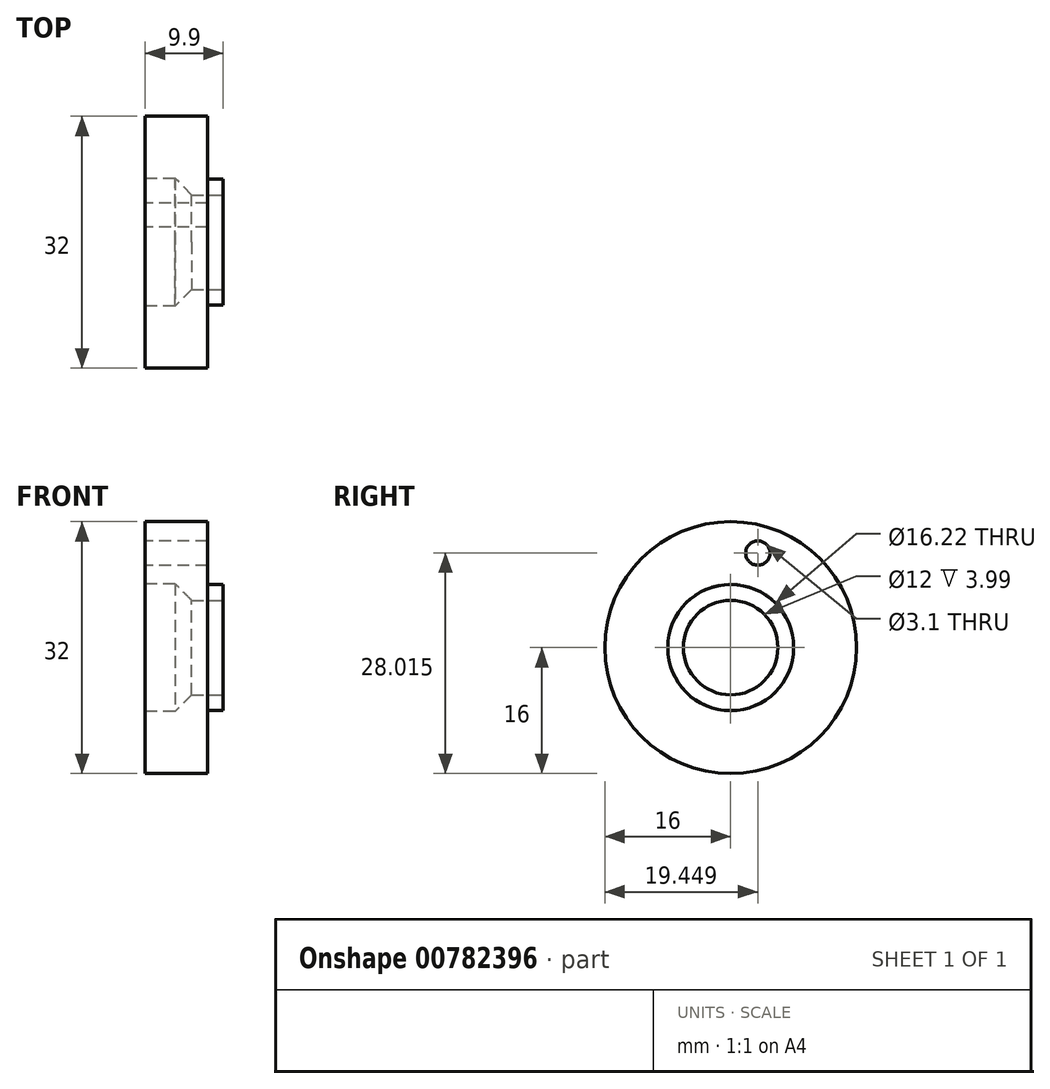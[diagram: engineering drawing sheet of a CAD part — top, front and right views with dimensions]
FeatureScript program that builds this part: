
annotation { "Feature Type Name" : "Feature", "Feature Type Description" : "" }
export const myFeature = defineFeature(function(context is Context, id is Id, definition is map)
    precondition{}
    {
        {
            var Q0;
            Q0=qCreatedBy(makeId("Right.planeOp"),FACE);
            var sketch = newSketch(context, id + "F0", { "sketchPlane" : qUnion([Q0])});
            skCircle(sketch, "E0", {"center": v(0, 0) * mm, "radius": 16 * mm});
            skSolve(sketch);
        }
        {
            var Q0;
            Q0 = qSketchRegion(id + "F0", true);
            extrude(context, id + "F1", {"entities" : qUnion([Q0]), "depth" : 7.9 * mm, "offsetDistance" : 25 * mm});
        }
        {
            var Q0;
            Q0=makeQuery(id+"F1.opExtrude","CAP_FACE",FACE,{"disambiguationData":[OSD([sQuery(id+"F0.wireOp",EDGE,"E0")])],"isStart":true});
            var sketch = newSketch(context, id + "F2", { "sketchPlane" : qUnion([Q0])});
            skCircle(sketch, "E1", {"center": v(0, 0) * mm, "radius": 8.1 * mm});
            skSolve(sketch);
        }
        {
            var Q0;
            Q0 = qSketchRegion(id + "F2", true);
            extrude(context, id + "F3", {"entities" : qUnion([Q0]), "operationType" : NewBodyOperationType.REMOVE, "oppositeDirection" : true, "depth" : 3.8 * mm, "offsetDistance" : 25 * mm});
        }
        {
            var Q0;
            Q0=makeQuery(id+"FPhex85518c5a8B_1.boolean.opBoolean","MERGE",FACE,{"derivedFrom":[makeQuery(id+"F1.opExtrude","CAP_FACE",FACE,{"disambiguationData":[OSD([sQuery(id+"F0.wireOp",EDGE,"E0"),sQuery(id+"F0.wireOp",EDGE,"LPqGSmC4-BEG3-Smh6-pqi2-9UDcotqoIPR3")])],"isStart":false}),makeQuery(id+"FPhex85518c5a8B_1.opExtrude","CAP_FACE",FACE,{"disambiguationData":[OSD([sQuery(id+"F5ubsA8xl3aw4eF_1.wireOp",EDGE,"xLex2xx2-WFXS-E97t-Ro50-xfE8aykVN3Uf")])],"isStart":true})]});
            var sketch = newSketch(context, id + "F4", { "sketchPlane" : qUnion([Q0])});
            skCircle(sketch, "E2", {"center": v(0, 0) * mm, "radius": 6 * mm});
            skSolve(sketch);
        }
        {
            var Q0;
            Q0 = qSketchRegion(id + "F4", true);
            extrude(context, id + "F5", {"entities" : qUnion([Q0]), "operationType" : NewBodyOperationType.REMOVE, "endBound" : BoundingType.THROUGH_ALL, "oppositeDirection" : true, "depth" : 25 * mm, "offsetDistance" : 25 * mm});
        }
        {
            var Q0;
            Q0=makeQuery(id+"F1.opExtrude","CAP_FACE",FACE,{"disambiguationData":[OSD([sQuery(id+"F0.wireOp",EDGE,"E0"),sQuery(id+"F0.wireOp",EDGE,"LPqGSmC4-BEG3-Smh6-pqi2-9UDcotqoIPR3")])],"isStart":true});
            var sketch = newSketch(context, id + "F6", { "sketchPlane" : qUnion([Q0])});
            skCircle(sketch, "E3", {"center": v(0, 0) * mm, "radius": 12.5 * mm, "construction": true});
            skCircle(sketch, "E4", {"center": v(-3.45, 12.01) * mm, "radius": 1.55 * mm});
            skSolve(sketch);
        }
        {
            var Q0;
            Q0=makeQuery(id+"F6.imprint","IMPRINT",FACE,{"disambiguationData":[TD([[makeQuery(id+"F6.imprint","IMPRINT",EDGE,{"derivedFrom":sQuery(id+"F6.wireOp",EDGE,"E4")}),1.0]])]});
            var Q1;
            Q1=sQuery(id+"F6.wireOp",EDGE,"E4");
            extrude(context, id + "F7", {"entities" : qUnion([Q0]), "operationType" : NewBodyOperationType.REMOVE, "surfaceEntities" : qUnion([Q1]), "endBound" : BoundingType.THROUGH_ALL, "oppositeDirection" : true, "depth" : 25 * mm, "offsetDistance" : 25 * mm});
        }
        {
            var Q0;
            Q0=makeQuery(id+"FPhex85518c5a8B_1.boolean.opBoolean","MERGE",FACE,{"derivedFrom":[makeQuery(id+"F1.opExtrude","CAP_FACE",FACE,{"disambiguationData":[OSD([sQuery(id+"F0.wireOp",EDGE,"E0"),sQuery(id+"F0.wireOp",EDGE,"LPqGSmC4-BEG3-Smh6-pqi2-9UDcotqoIPR3")])],"isStart":false}),makeQuery(id+"FPhex85518c5a8B_1.opExtrude","CAP_FACE",FACE,{"disambiguationData":[OSD([sQuery(id+"F5ubsA8xl3aw4eF_1.wireOp",EDGE,"xLex2xx2-WFXS-E97t-Ro50-xfE8aykVN3Uf")])],"isStart":true})]});
            var sketch = newSketch(context, id + "F8", { "sketchPlane" : qUnion([Q0])});
            skCircle(sketch, "E5", {"center": v(0, 0) * mm, "radius": 6 * mm});
            skCircle(sketch, "E6", {"center": v(0, 0) * mm, "radius": 8 * mm});
            skSolve(sketch);
        }
        {
            var Q0;
            Q0=makeQuery(id+"F8.imprint","IMPRINT",FACE,{"disambiguationData":[TD([[makeQuery(id+"F8.imprint","IMPRINT",EDGE,{"derivedFrom":sQuery(id+"F8.wireOp",EDGE,"E5")}),-1.0]])]});
            extrude(context, id + "F9", {"entities" : qUnion([Q0]), "operationType" : NewBodyOperationType.ADD, "depth" : 2 * mm, "offsetDistance" : 25 * mm});
        }
        {
            var Q0;
            Q0=makeQuery(id+"F5.boolean.opBoolean","INTERSECT",EDGE,{"derivedFrom":[makeQuery(id+"F3.boolean.opBoolean","COPY",FACE,{"derivedFrom":makeQuery(id+"F3.opExtrude","CAP_FACE",FACE,{"disambiguationData":[OSD([sQuery(id+"F2.wireOp",EDGE,"E1")])],"isStart":false})}),makeQuery(id+"F5.opExtrude","SWEPT_FACE",FACE,{"disambiguationData":[OSD([sQuery(id+"F4.wireOp",EDGE,"E2")])]})]});
            chamfer(context, id + "F10", {"entities" : qUnion([Q0]), "chamferType" : ChamferType.OFFSET_ANGLE, "width" : 2.1 * mm, "oppositeDirection" : false, "angle" : 45 * degree, "tangentPropagation" : true});
        }
    });
